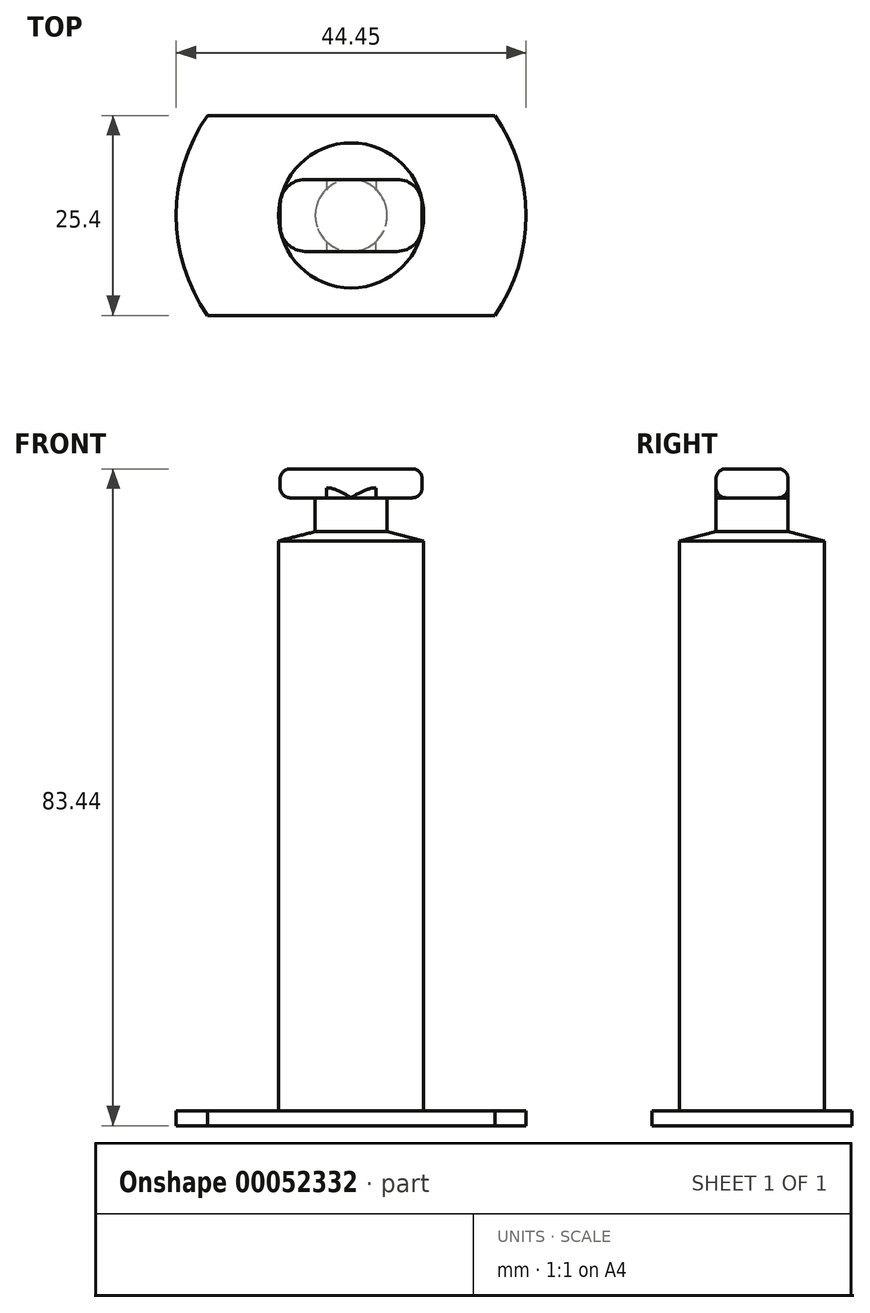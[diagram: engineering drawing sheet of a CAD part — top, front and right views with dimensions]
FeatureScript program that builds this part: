
annotation { "Feature Type Name" : "Feature", "Feature Type Description" : "" }
export const myFeature = defineFeature(function(context is Context, id is Id, definition is map)
    precondition{}
    {
        {
            var Q0;
            Q0=qCreatedBy(makeId("Top.planeOp"),FACE);
            var sketch = newSketch(context, id + "F0", { "sketchPlane" : qUnion([Q0])});
            skCircle(sketch, "E0", {"center": v(0, 0) * mm, "radius": 9.2 * mm});
            skSolve(sketch);
        }
        {
            var Q0;
            Q0=makeQuery(id+"F0.imprint","IMPRINT",FACE,{"disambiguationData":[TD([[makeQuery(id+"F0.imprint","IMPRINT",EDGE,{"derivedFrom":sQuery(id+"F0.wireOp",EDGE,"E0")}),1.0]])]});
            extrude(context, id + "F1", {"entities" : qUnion([Q0]), "depth" : 73.66 * mm});
        }
        {
            var Q0;
            Q0=makeQuery(id+"F1.opExtrude","CAP_FACE",FACE,{"disambiguationData":[OSD([sQuery(id+"F0.wireOp",EDGE,"E0")])],"isStart":false});
            var sketch = newSketch(context, id + "F2", { "sketchPlane" : qUnion([Q0])});
            skCircle(sketch, "E1", {"center": v(0, 0) * mm, "radius": 4.57 * mm});
            skSolve(sketch);
        }
        {
            var Q0;
            Q0=makeQuery(id+"F2.imprint","IMPRINT",FACE,{"disambiguationData":[TD([[makeQuery(id+"F2.imprint","IMPRINT",EDGE,{"derivedFrom":sQuery(id+"F2.wireOp",EDGE,"E1")}),1.0]])]});
            extrude(context, id + "F3", {"entities" : qUnion([Q0]), "operationType" : NewBodyOperationType.ADD, "depth" : 4.2 * mm});
        }
        {
            var Q0;
            Q0=makeQuery(id+"F3.opExtrude","CAP_FACE",FACE,{"disambiguationData":[OSD([sQuery(id+"F2.wireOp",EDGE,"E1")])],"isStart":false});
            var sketch = newSketch(context, id + "F4", { "sketchPlane" : qUnion([Q0])});
            skLineSegment(sketch, "E2.rect.bottom", {"start": v(-9.02, 4.57) * mm, "end": v(9.02, 4.57) * mm});
            skLineSegment(sketch, "E2.rect.top", {"start": v(-9.02, -4.57) * mm, "end": v(9.02, -4.57) * mm});
            skLineSegment(sketch, "E2.rect.left", {"start": v(-9.02, 4.57) * mm, "end": v(-9.02, -4.57) * mm});
            skLineSegment(sketch, "E2.rect.right", {"start": v(9.02, 4.57) * mm, "end": v(9.02, -4.57) * mm});
            skPoint(sketch, "E2.rect.middle", {"position": v(0, 0) * mm});
            skSolve(sketch);
        }
        {
            var Q0;
            {var subQ0=sQuery(id+"F4.wireOp",EDGE,"E2.rect.left");Q0=makeQuery(id+"F4.imprint","IMPRINT",FACE,{"disambiguationData":[TD([[makeQuery(id+"F4.imprint","IMPRINT",EDGE,{"derivedFrom":subQ0}),1.0]])]});}
            var Q1;
            {var subQ0=sQuery(id+"F4.wireOp",EDGE,"E2.rect.right");Q1=makeQuery(id+"F4.imprint","IMPRINT",FACE,{"disambiguationData":[TD([[makeQuery(id+"F4.imprint","IMPRINT",EDGE,{"derivedFrom":subQ0}),-1.0]])]});}
            var Q2;
            {var subQ0=makeQuery(id+"F3.opExtrude","CAP_EDGE",EDGE,{"disambiguationData":[OSD([sQuery(id+"F2.wireOp",EDGE,"E1")])],"isStart":false});var subQ1=makeQuery(id+"F4.imprint","INTERSECT",VERTEX,{"derivedFrom":[subQ0,sQuery(id+"F4.wireOp",EDGE,"E2.rect.bottom")]});Q2=makeQuery(id+"F4.imprint","IMPRINT",FACE,{"disambiguationData":[TD([[makeQuery(id+"F4.imprint","IMPRINT",EDGE,{"disambiguationData":[TD([[subQ1,-1.0]])],"derivedFrom":subQ0}),1.0]])]});}
            extrude(context, id + "F5", {"entities" : qUnion([Q0, Q1, Q2]), "operationType" : NewBodyOperationType.ADD, "depth" : 3.68 * mm});
        }
        {
            var Q0;
            Q0=makeQuery(id+"F5.opExtrude","SWEPT_EDGE",EDGE,{"disambiguationData":[OSD([sQuery(id+"F4.wireOp",EDGE,"E2.rect.bottom"),sQuery(id+"F4.wireOp",EDGE,"E2.rect.left")])]});
            var Q1;
            Q1=makeQuery(id+"F5.opExtrude","SWEPT_EDGE",EDGE,{"disambiguationData":[OSD([sQuery(id+"F4.wireOp",EDGE,"E2.rect.top"),sQuery(id+"F4.wireOp",EDGE,"E2.rect.left")])]});
            var Q2;
            Q2=makeQuery(id+"F5.opExtrude","SWEPT_EDGE",EDGE,{"disambiguationData":[OSD([sQuery(id+"F4.wireOp",EDGE,"E2.rect.bottom"),sQuery(id+"F4.wireOp",EDGE,"E2.rect.right")])]});
            var Q3;
            Q3=makeQuery(id+"F5.opExtrude","SWEPT_EDGE",EDGE,{"disambiguationData":[OSD([sQuery(id+"F4.wireOp",EDGE,"E2.rect.top"),sQuery(id+"F4.wireOp",EDGE,"E2.rect.right")])]});
            fillet(context, id + "F6", {"entities" : qUnion([Q0, Q1, Q2, Q3]), "radius" : 3.17 * mm, "tangentPropagation" : true, "allowEdgeOverflow" : false});
        }
        {
            var Q0;
            Q0=makeQuery(id+"F1.opExtrude","CAP_EDGE",EDGE,{"disambiguationData":[OSD([sQuery(id+"F0.wireOp",EDGE,"E0")])],"isStart":false});
            chamfer(context, id + "F7", {"entities" : qUnion([Q0]), "chamferType" : ChamferType.TWO_OFFSETS, "width1" : 5.08 * mm, "oppositeDirection" : false, "width2" : 1.27 * mm, "tangentPropagation" : true});
        }
        {
            var Q0;
            {var subQ0=sQuery(id+"F4.wireOp",EDGE,"E2.rect.top");var subQ1=sQuery(id+"F4.wireOp",EDGE,"E2.rect.right");var subQ2=sQuery(id+"F4.wireOp",EDGE,"E2.rect.bottom");var subQ3=makeQuery(id+"F5.opExtrude","CAP_FACE",FACE,{"disambiguationData":[OSD([subQ2,subQ0,sQuery(id+"F4.wireOp",EDGE,"E2.rect.left"),subQ1])],"isStart":true});Q0=makeQuery(id+"F6.opFillet","BLEND_EDGE",EDGE,{"blendedFrom":[makeQuery(id+"F5.opExtrude","SWEPT_EDGE",EDGE,{"disambiguationData":[OSD([subQ2,subQ1])]}),makeQuery(id+"F5.boolean.opBoolean","SPLIT",FACE,{"disambiguationData":[TD([makeQuery(id+"F5.opExtrude","SWEPT_FACE",FACE,{"disambiguationData":[OSD([subQ1])]})])],"derivedFrom":subQ3})],"blendedInto":[makeQuery(id+"F5.boolean.opBoolean","SPLIT",FACE,{"disambiguationData":[TD([makeQuery(id+"F5.opExtrude","SWEPT_FACE",FACE,{"disambiguationData":[OSD([subQ1])]})])],"derivedFrom":subQ3})]});}
            var Q1;
            Q1=makeQuery(id+"F5.opExtrude","CAP_EDGE",EDGE,{"disambiguationData":[OSD([sQuery(id+"F4.wireOp",EDGE,"E2.rect.bottom")])],"isStart":false});
            fillet(context, id + "F8", {"entities" : qUnion([Q0, Q1]), "radius" : 1.27 * mm, "tangentPropagation" : true, "allowEdgeOverflow" : false});
        }
        {
            var Q0;
            Q0=makeQuery(id+"F1.opExtrude","CAP_FACE",FACE,{"disambiguationData":[OSD([sQuery(id+"F0.wireOp",EDGE,"E0")])],"isStart":true});
            var sketch = newSketch(context, id + "F9", { "sketchPlane" : qUnion([Q0])});
            skCircle(sketch, "E3", {"center": v(0, 0) * mm, "radius": 22.23 * mm});
            skLineSegment(sketch, "E4", {"start": v(18.24, -12.7) * mm, "end": v(-18.24, -12.7) * mm});
            skLineSegment(sketch, "E5", {"start": v(-18.24, 12.7) * mm, "end": v(18.24, 12.7) * mm});
            skSolve(sketch);
        }
        {
            var Q0;
            Q0=makeQuery(id+"F9.imprint","IMPRINT",FACE,{"disambiguationData":[TD([[makeQuery(id+"F9.imprint","IMPRINT",EDGE,{"derivedFrom":sQuery(id+"F9.wireOp",EDGE,"E3")}),1.0]])]});
            var Q1;
            Q1=makeQuery(id+"F9.imprint","IMPRINT",FACE,{"disambiguationData":[TD([[makeQuery(id+"F9.imprint","IMPRINT",EDGE,{"derivedFrom":makeQuery(id+"F1.opExtrude","CAP_EDGE",EDGE,{"disambiguationData":[OSD([sQuery(id+"F0.wireOp",EDGE,"E0")])],"isStart":true})}),-1.0]])]});
            extrude(context, id + "F10", {"entities" : qUnion([Q0, Q1]), "operationType" : NewBodyOperationType.ADD, "depth" : 1.9 * mm});
        }
    });
